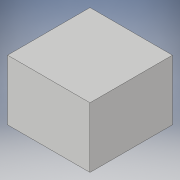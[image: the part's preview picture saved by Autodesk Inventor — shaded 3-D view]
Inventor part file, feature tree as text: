
AUTODESK INVENTOR PART (.ipt)
format: ipt  version: 2019 (Build 230136000, 136)  size: 111,104 bytes
history: native  units: mm
features: extrude x3, sketch x3
ambient origin geometry x8: Origin, YZ Plane, XZ Plane, XY Plane, X Axis, Y Axis, Z Axis, Center Point
bodies: Solid1 (feature_tree)
feature tree (6):
  extrude  "Extrusion1"  Depth=20.5mm
  extrude  "Extrusion2"  Depth=3.0mm
  extrude  "Extrusion3"  Depth=3.0mm TaperAngle=0.0deg
  sketch  "Sketch1"  dims[d0=1.5mm d1=20.5mm]
  sketch  "Sketch2"  dims[d2=7.0mm d3=0.0mm d4=3.0mm]
  sketch  "Sketch3"  dims[d5=5.0mm d6=0.0mm d7=3.0mm d8=0.0mm]
